# Revit family: Facade_60_Curtain_Wall_S23_Standard
name_source: partatom
category: Windows
revit_build: Autodesk Revit 2014 (Build: 20130308_1515(x64)
units: mm (PartAtom-declared; Revit-internal decimal feet)

## types (32) — shared parameters
DG Gasket Thickness = 12 mm  [stored 0.0393701 ft]
Description = Curtain wall, S23
Frame Bottom Gap = 30 mm  [stored 0.0984252 ft]
Frame Thickness = 102 mm
Glazing Bottom Gap = 70 mm
Glazing Side Gap = 40 mm  [stored 0.131234 ft]
Glazing Top Gap = 40 mm  [stored 0.131234 ft]
Half Expansion Break = No
Jamb Width = 60 mm  [stored 0.19685 ft]
Limit Door Height Max = 18149 mm
Limit Door Height Min = 1049 mm
Limit Door Width Max = 6099 mm
Limit Door Width Min = 699 mm
Limit Panel Height Max = 6000 mm  [stored 19.685 ft]
Limit Panel Height Min = 300 mm  [stored 0.984252 ft]
Limit Panel Width Max = 3000 mm  [stored 9.84252 ft]
Limit Panel Width Min = 300 mm  [stored 0.984252 ft]
Manufacturer = Crealco
Max System DG Unit Thickness = 25 mm  [stored 0.082021 ft]
Model = Façade 60
Quarter Expansion Break = No
Sill Height = 85 mm  [stored 0.278871 ft]
Thermal Break Material = Plastic, Opaque Black
Top Profile Overhang = 6 mm  [stored 0.019685 ft]
URL = http://www.crealco.co.za
Wall Closure = By host
zero-valued in all types: Custom Offset From Exterior, Default Sill Height

## per-type parameters (varying)
| type | Custom Curtain Wall Height | Custom Curtain Wall Width | Custom Windload | Intruderprufe Insulated LowE SHGC Value | Intruderprufe Insulated LowE U Value | Intruderprufe Insulated SHGC Value | Intruderprufe Insulated U Value | Intruderprufe LowE SHGC Value | Intruderprufe LowE U Value | Intruderprufe SHGC Value | Intruderprufe U Value |
| F60-S23-1825-1000Pa | 2490 mm | 1790 mm  [stored 5.8727 ft] | 1000 mm  [stored 3.28084 ft] | 0.515 | 2.59 | 0.572 | 3.18 | 0.581 | 4.43 | 0.663 | 5.66 |
| F60-S23-1825-1500Pa | 2490 mm | 1790 mm  [stored 5.8727 ft] | 1500 mm  [stored 4.92126 ft] | 0.515 | 2.59 | 0.572 | 3.18 | 0.581 | 4.43 | 0.663 | 5.66 |
| F60-S23-1825-2000Pa | 2490 mm | 1790 mm  [stored 5.8727 ft] | 2000 mm  [stored 6.56168 ft] | 0.515 | 2.59 | 0.572 | 3.18 | 0.581 | 4.43 | 0.663 | 5.66 |
| F60-S23-2425-1000Pa | 2490 mm | 2390 mm  [stored 7.84121 ft] | 1000 mm  [stored 3.28084 ft] | 0.521 | 2.56 | 0.578 | 3.15 | 0.5888 | 4.4 | 0.67 | 5.98 |
| F60-S23-2425-1500Pa | 2490 mm | 2390 mm  [stored 7.84121 ft] | 1500 mm  [stored 4.92126 ft] | 0.521 | 2.56 | 0.578 | 3.15 | 0.5888 | 4.4 | 0.67 | 5.98 |
| F60-S23-2425-2000Pa | 2490 mm | 2390 mm  [stored 7.84121 ft] | 2000 mm  [stored 6.56168 ft] | 0.521 | 2.56 | 0.578 | 3.15 | 0.5888 | 4.4 | 0.67 | 5.98 |
| F60-S23-3025-1000Pa | 2490 mm | 2990 mm | 1000 mm  [stored 3.28084 ft] | 0.529 | 2.51 | 0.587 | 3.12 | 0.597 | 4.36 | 0.681 | 5.7 |
| F60-S23-3025-1500Pa | 2490 mm | 2990 mm | 1500 mm  [stored 4.92126 ft] | 0.529 | 2.51 | 0.587 | 3.12 | 0.597 | 4.36 | 0.681 | 5.7 |
| F60-S23-3025-2000Pa | 2490 mm | 2990 mm | 2000 mm  [stored 6.56168 ft] | 0.529 | 2.51 | 0.587 | 3.12 | 0.597 | 4.36 | 0.681 | 5.7 |
| F60-S23-3625-1000Pa | 2490 mm | 3590 mm | 1000 mm  [stored 3.28084 ft] | 0.534 | 2.048 | 0.592 | 3.1 | 0.603 | 4.34 | 0.688 | 5.7 |
| F60-S23-3625-1500Pa | 2490 mm | 3590 mm | 1500 mm  [stored 4.92126 ft] | 0.534 | 2.048 | 0.592 | 3.1 | 0.603 | 4.34 | 0.688 | 5.7 |
| F60-S23-3625-2000Pa | 2490 mm | 3590 mm | 2000 mm  [stored 6.56168 ft] | 0.534 | 2.048 | 0.592 | 3.1 | 0.603 | 4.34 | 0.688 | 5.7 |
| F60-S23-4225-1000Pa | 2490 mm | 4190 mm  [stored 13.7467 ft] | 1000 mm  [stored 3.28084 ft] | 0.538 | 2.45 | 0.596 | 3.08 | 0.607 | 4.32 | 0.693 | 5.72 |
| F60-S23-4225-1500Pa | 2490 mm | 4190 mm  [stored 13.7467 ft] | 1500 mm  [stored 4.92126 ft] | 0.538 | 2.45 | 0.596 | 3.08 | 0.607 | 4.32 | 0.693 | 5.72 |
| F60-S23-4225-2000Pa | 2490 mm | 4190 mm  [stored 13.7467 ft] | 2000 mm  [stored 6.56168 ft] | 0.538 | 2.45 | 0.596 | 3.08 | 0.607 | 4.32 | 0.693 | 5.72 |
| F60-S23-4825-1000Pa | 2490 mm | 4790 mm  [stored 15.7152 ft] | 1000 mm  [stored 3.28084 ft] | 0.54 | 2.44 | 0.6 | 3.07 | 0.61 | 4.31 | 0.696 | 5.73 |
| F60-S23-4825-1500Pa | 2490 mm | 4790 mm  [stored 15.7152 ft] | 1500 mm  [stored 4.92126 ft] | 0.54 | 2.44 | 0.6 | 3.07 | 0.61 | 4.31 | 0.696 | 5.73 |
| F60-S23-4825-2000Pa | 2490 mm | 4790 mm  [stored 15.7152 ft] | 2000 mm  [stored 6.56168 ft] | 0.54 | 2.44 | 0.6 | 3.07 | 0.61 | 4.31 | 0.696 | 5.73 |
| F60-S23-5425-1000Pa | 2490 mm | 5390 mm  [stored 17.6837 ft] | 1000 mm  [stored 3.28084 ft] | 0.543 | 2.42 | 0.602 | 3.06 | 0.613 | 4.3 | 0.699 | 5.74 |
| F60-S23-5425-1500Pa | 2490 mm | 5390 mm  [stored 17.6837 ft] | 1500 mm  [stored 4.92126 ft] | 0.543 | 2.42 | 0.602 | 3.06 | 0.613 | 4.3 | 0.699 | 5.74 |
| F60-S23-5425-2000Pa | 2490 mm | 5390 mm  [stored 17.6837 ft] | 2000 mm  [stored 6.56168 ft] | 0.543 | 2.42 | 0.602 | 3.06 | 0.613 | 4.3 | 0.699 | 5.74 |
| F60-S23-6025-1000Pa | 2490 mm | 599 mm  [stored 1.96522 ft] | 1000 mm  [stored 3.28084 ft] | 0.544 | 2.41 | 0.604 | 3.05 | 0.615 | 4.29 | 0.701 | 5.74 |
| F60-S23-6025-1500Pa | 2490 mm | 599 mm  [stored 1.96522 ft] | 1500 mm  [stored 4.92126 ft] | 0.544 | 2.41 | 0.604 | 3.05 | 0.615 | 4.29 | 0.701 | 5.74 |
| F60-S23-6025-2000Pa | 2490 mm | 599 mm  [stored 1.96522 ft] | 2000 mm  [stored 6.56168 ft] | 0.544 | 2.41 | 0.604 | 3.05 | 0.615 | 4.29 | 0.701 | 5.74 |
| F60-S23-1850-1000Pa | 4990 mm  [stored 16.3714 ft] | 1790 mm  [stored 5.8727 ft] | 1000 mm  [stored 3.28084 ft] | 0.532 | 2.48 | 0.59 | 3.1 | 0.6 | 4.28 | 0.685 | 5.64 |
| F60-S23-1850-1500Pa | 4990 mm  [stored 16.3714 ft] | 1790 mm  [stored 5.8727 ft] | 1500 mm  [stored 4.92126 ft] | 0.532 | 2.48 | 0.59 | 3.1 | 0.6 | 4.28 | 0.685 | 5.64 |
| F60-S23-1850-2000Pa | 4990 mm  [stored 16.3714 ft] | 1790 mm  [stored 5.8727 ft] | 2000 mm  [stored 6.56168 ft] | 0.532 | 2.48 | 0.59 | 3.1 | 0.6 | 4.28 | 0.685 | 5.64 |
| F60-S23-2450-1000Pa | 4990 mm  [stored 16.3714 ft] | 2390 mm  [stored 7.84121 ft] | 1000 mm  [stored 3.28084 ft] | 0.537 | 2.44 | 0.596 | 3.07 | 0.607 | 4.25 | 0.692 | 5.66 |
| F60-S23-2450-1500Pa | 4990 mm  [stored 16.3714 ft] | 2390 mm  [stored 7.84121 ft] | 1500 mm  [stored 4.92126 ft] | 0.537 | 2.44 | 0.596 | 3.07 | 0.607 | 4.25 | 0.692 | 5.66 |
| F60-S23-3050-1000Pa | 4990 mm  [stored 16.3714 ft] | 2990 mm | 1000 mm  [stored 3.28084 ft] | 0.546 | 2.39 | 0.605 | 3.04 | 0.616 | 4.21 | 0.703 | 5.68 |
| F60-S23-3650-1000Pa | 4990 mm  [stored 16.3714 ft] | 3590 mm | 1000 mm  [stored 3.28084 ft] | 0.551 | 2.36 | 0.611 | 3.01 | 0.622 | 4.19 | 0.71 | 5.7 |
| F60-S23-4250-1000Pa | 4990 mm  [stored 16.3714 ft] | 4190 mm  [stored 13.7467 ft] | 1000 mm  [stored 3.28084 ft] | 0.555 | 2.34 | 0.616 | 3 | 0.627 | 4.17 | 0.716 | 5.71 |

note: [stored X ft] marks values corroborated as IEEE doubles in the binary element streams (Revit-internal decimal feet)

## geometry (parser evidence)
native form markers: Sweep x18
no freeform markers — native parametric forms only
